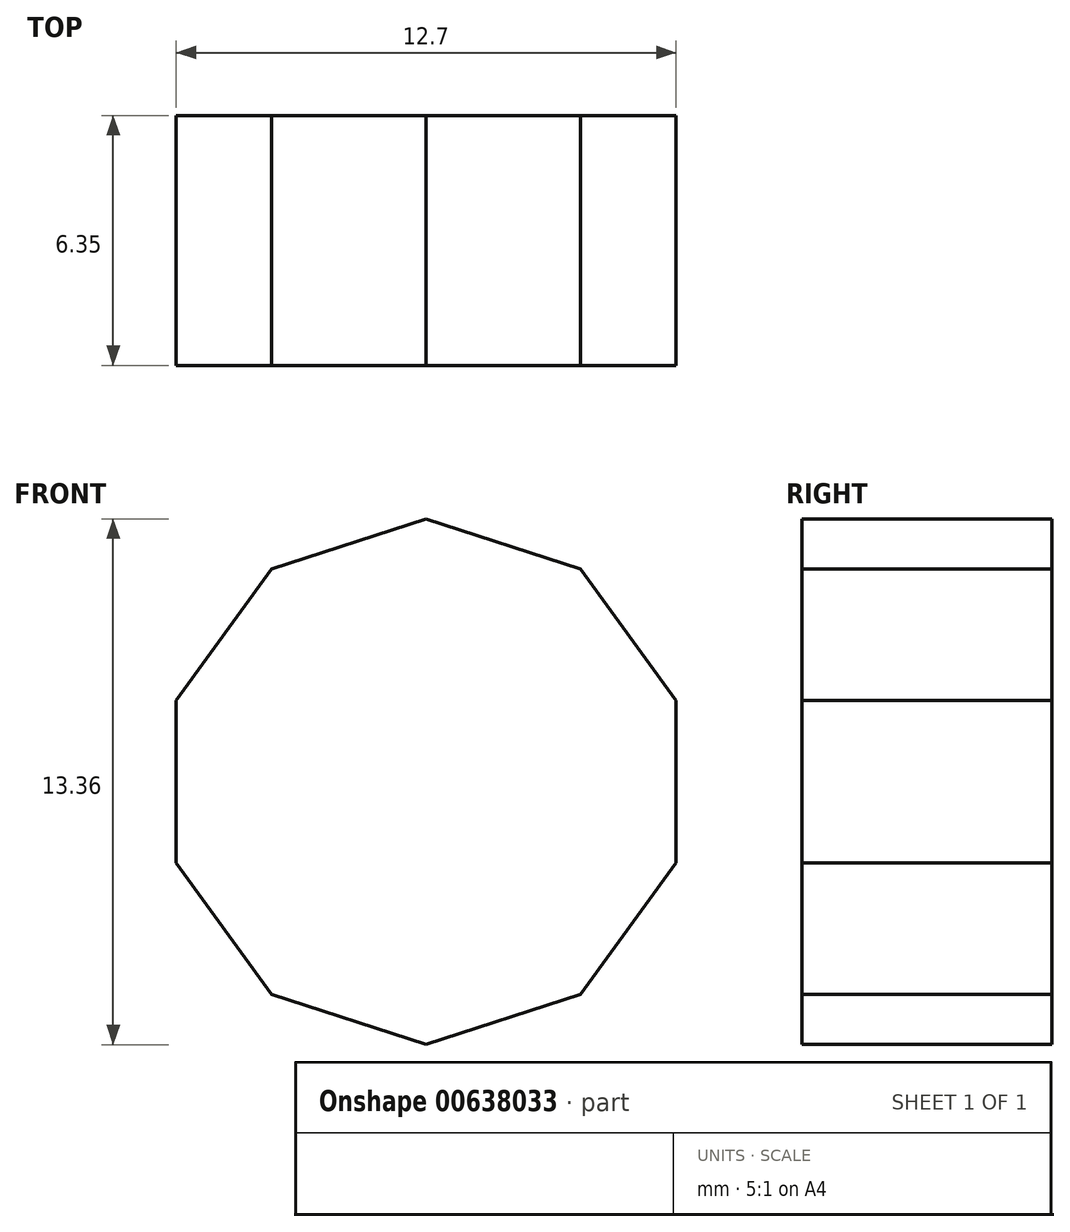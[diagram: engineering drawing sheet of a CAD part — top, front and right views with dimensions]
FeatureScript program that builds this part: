
annotation { "Feature Type Name" : "Feature", "Feature Type Description" : "" }
export const myFeature = defineFeature(function(context is Context, id is Id, definition is map)
    precondition{}
    {
        {
            var Q0;
            Q0=qCreatedBy(makeId("Front.planeOp"),FACE);
            var sketch = newSketch(context, id + "F0", { "sketchPlane" : qUnion([Q0])});
            skCircle(sketch, "E0.cCircle", {"center": v(0, 0) * mm, "radius": 6.35 * mm, "construction": true});
            skLineSegment(sketch, "E0.0", {"start": v(6.35, 2.06) * mm, "end": v(6.35, -2.06) * mm});
            skLineSegment(sketch, "E0.1", {"start": v(6.35, -2.06) * mm, "end": v(3.92, -5.4) * mm});
            skLineSegment(sketch, "E0.2", {"start": v(3.92, -5.4) * mm, "end": v(0, -6.68) * mm});
            skLineSegment(sketch, "E0.3", {"start": v(0, -6.68) * mm, "end": v(-3.92, -5.4) * mm});
            skLineSegment(sketch, "E0.4", {"start": v(-3.92, -5.4) * mm, "end": v(-6.35, -2.06) * mm});
            skLineSegment(sketch, "E0.5", {"start": v(-6.35, -2.06) * mm, "end": v(-6.35, 2.06) * mm});
            skLineSegment(sketch, "E0.6", {"start": v(-6.35, 2.06) * mm, "end": v(-3.92, 5.4) * mm});
            skLineSegment(sketch, "E0.7", {"start": v(-3.92, 5.4) * mm, "end": v(0, 6.68) * mm});
            skLineSegment(sketch, "E0.8", {"start": v(0, 6.68) * mm, "end": v(3.92, 5.4) * mm});
            skLineSegment(sketch, "E0.9", {"start": v(3.92, 5.4) * mm, "end": v(6.35, 2.06) * mm});
            skPoint(sketch, "E0.0.midPoint", {"position": v(6.35, 0) * mm});
            skSolve(sketch);
        }
        {
            var Q0;
            Q0=makeQuery(id+"F0.imprint","IMPRINT",FACE,{"disambiguationData":[TD([[makeQuery(id+"F0.imprint","IMPRINT",EDGE,{"derivedFrom":sQuery(id+"F0.wireOp",EDGE,"E0.0")}),-1.0]])]});
            extrude(context, id + "F1", {"entities" : qUnion([Q0]), "depth" : 6.35 * mm, "offsetDistance" : 25.4 * mm});
        }
        {
            var Q0;
            Q0=makeQuery(id+"F1.opExtrude","SWEPT_FACE",FACE,{"disambiguationData":[OSD([sQuery(id+"F0.wireOp",EDGE,"E0.8")])]});
            var sketch = newSketch(context, id + "F2", { "sketchPlane" : qUnion([Q0])});
            skLineSegment(sketch, "E1", {"start": v(0, 0) * mm, "end": v(0, -6.35) * mm});
            skLineSegment(sketch, "E2", {"start": v(1.63, -1.23) * mm, "end": v(-1.63, -5.12) * mm});
            skPoint(sketch, "E3", {"position": v(0, -3.18) * mm});
            skFitSpline(sketch, "E4", {"points": [v(1.63, -1.23) * mm, v(1.63, -2.95) * mm, v(-1.63, -5.12) * mm, v(-0.55, -4.1) * mm, v(0.85, -2.62) * mm, v(1.63, -1.23) * mm]});
            skSolve(sketch);
        }
        {
            var Q0;
            Q0=makeQuery(id+"F1.opExtrude","SWEPT_FACE",FACE,{"disambiguationData":[OSD([sQuery(id+"F0.wireOp",EDGE,"E0.7")])]});
            var sketch = newSketch(context, id + "F3", { "sketchPlane" : qUnion([Q0])});
            skLineSegment(sketch, "E5", {"start": v(-0.1, 0.06) * mm, "end": v(-0.1, -6.29) * mm});
            skLineSegment(sketch, "E6", {"start": v(1.53, -1.17) * mm, "end": v(-1.74, -5.06) * mm});
            skPoint(sketch, "E7", {"position": v(-0.1, -3.11) * mm});
            skFitSpline(sketch, "E8", {"points": [v(1.53, -1.17) * mm, v(1.53, -2.88) * mm, v(-1.74, -5.06) * mm, v(-0.65, -4.03) * mm, v(0.75, -2.56) * mm, v(1.53, -1.17) * mm]});
            skSolve(sketch);
        }
        {
            var Q0;
            Q0=makeQuery(id+"F1.opExtrude","SWEPT_FACE",FACE,{"disambiguationData":[OSD([sQuery(id+"F0.wireOp",EDGE,"E0.6")])]});
            var sketch = newSketch(context, id + "F4", { "sketchPlane" : qUnion([Q0])});
            skLineSegment(sketch, "E9", {"start": v(-0.02, -0.43) * mm, "end": v(6.33, -0.43) * mm});
            skLineSegment(sketch, "E10", {"start": v(1.21, 1.2) * mm, "end": v(5.1, -2.06) * mm});
            skFitSpline(sketch, "E11", {"points": [v(1.21, 1.2) * mm, v(2.93, 1.2) * mm, v(5.1, -2.06) * mm, v(4.08, -0.98) * mm, v(2.6, 0.42) * mm, v(1.21, 1.2) * mm]});
            skSolve(sketch);
        }
        {
            var Q0;
            Q0=makeQuery(id+"F1.opExtrude","SWEPT_FACE",FACE,{"disambiguationData":[OSD([sQuery(id+"F0.wireOp",EDGE,"E0.5")])]});
            var sketch = newSketch(context, id + "F5", { "sketchPlane" : qUnion([Q0])});
            skLineSegment(sketch, "E12", {"start": v(6.35, 0) * mm, "end": v(0, 0) * mm});
            skLineSegment(sketch, "E13", {"start": v(0.01, 0) * mm, "end": v(6.36, 0) * mm});
            skLineSegment(sketch, "E14", {"start": v(1.24, 1.63) * mm, "end": v(5.13, -1.63) * mm});
            skFitSpline(sketch, "E15", {"points": [v(1.24, 1.63) * mm, v(2.96, 1.63) * mm, v(5.13, -1.63) * mm, v(4.1, -0.55) * mm, v(2.64, 0.85) * mm, v(1.24, 1.63) * mm]});
            skSolve(sketch);
        }
        {
            var Q0;
            Q0=makeQuery(id+"F1.opExtrude","SWEPT_FACE",FACE,{"disambiguationData":[OSD([sQuery(id+"F0.wireOp",EDGE,"E0.4")])]});
            var sketch = newSketch(context, id + "F6", { "sketchPlane" : qUnion([Q0])});
            skLineSegment(sketch, "E16", {"start": v(6.35, 0) * mm, "end": v(0, 0) * mm});
            skLineSegment(sketch, "E17", {"start": v(0, 0) * mm, "end": v(6.34, 0) * mm});
            skLineSegment(sketch, "E18", {"start": v(1.22, 1.63) * mm, "end": v(5.12, -1.63) * mm});
            skFitSpline(sketch, "E19", {"points": [v(1.22, 1.63) * mm, v(2.94, 1.63) * mm, v(5.12, -1.63) * mm, v(4.09, -0.55) * mm, v(2.62, 0.85) * mm, v(1.22, 1.63) * mm]});
            skSolve(sketch);
        }
        {
            var Q0;
            Q0=makeQuery(id+"F1.opExtrude","SWEPT_FACE",FACE,{"disambiguationData":[OSD([sQuery(id+"F0.wireOp",EDGE,"E0.3")])]});
            var sketch = newSketch(context, id + "F7", { "sketchPlane" : qUnion([Q0])});
            skLineSegment(sketch, "E20", {"start": v(0, 6.35) * mm, "end": v(0, 0) * mm});
            skLineSegment(sketch, "E21", {"start": v(0, -0.02) * mm, "end": v(0, 6.33) * mm});
            skLineSegment(sketch, "E22", {"start": v(-1.63, 1.21) * mm, "end": v(1.63, 5.1) * mm});
            skFitSpline(sketch, "E23", {"points": [v(-1.63, 1.21) * mm, v(-1.63, 2.93) * mm, v(1.63, 5.1) * mm, v(0.55, 4.08) * mm, v(-0.85, 2.6) * mm, v(-1.63, 1.21) * mm]});
            skSolve(sketch);
        }
        {
            var Q0;
            Q0=makeQuery(id+"F1.opExtrude","SWEPT_FACE",FACE,{"disambiguationData":[OSD([sQuery(id+"F0.wireOp",EDGE,"E0.2")])]});
            var sketch = newSketch(context, id + "F8", { "sketchPlane" : qUnion([Q0])});
            skLineSegment(sketch, "E24", {"start": v(0, 6.35) * mm, "end": v(0, 0) * mm});
            skLineSegment(sketch, "E25", {"start": v(0, 0) * mm, "end": v(0, 6.36) * mm});
            skLineSegment(sketch, "E26", {"start": v(-1.63, 1.23) * mm, "end": v(1.63, 5.13) * mm});
            skFitSpline(sketch, "E27", {"points": [v(-1.63, 1.23) * mm, v(-1.63, 2.95) * mm, v(1.63, 5.13) * mm, v(0.55, 4.1) * mm, v(-0.85, 2.63) * mm, v(-1.63, 1.23) * mm]});
            skSolve(sketch);
        }
        {
            var Q0;
            Q0=makeQuery(id+"F1.opExtrude","SWEPT_FACE",FACE,{"disambiguationData":[OSD([sQuery(id+"F0.wireOp",EDGE,"E0.1")])]});
            var sketch = newSketch(context, id + "F9", { "sketchPlane" : qUnion([Q0])});
            skLineSegment(sketch, "E28", {"start": v(-6.35, 0) * mm, "end": v(0, 0) * mm});
            skLineSegment(sketch, "E29", {"start": v(0, 0) * mm, "end": v(-6.35, 0) * mm});
            skLineSegment(sketch, "E30", {"start": v(-1.23, -1.63) * mm, "end": v(-5.12, 1.63) * mm});
            skFitSpline(sketch, "E31", {"points": [v(-1.23, -1.63) * mm, v(-2.95, -1.63) * mm, v(-5.12, 1.63) * mm, v(-4.1, 0.55) * mm, v(-2.62, -0.85) * mm, v(-1.23, -1.63) * mm]});
            skSolve(sketch);
        }
        {
            var Q0;
            Q0=makeQuery(id+"F1.opExtrude","SWEPT_FACE",FACE,{"disambiguationData":[OSD([sQuery(id+"F0.wireOp",EDGE,"E0.0")])]});
            var sketch = newSketch(context, id + "F10", { "sketchPlane" : qUnion([Q0])});
            skLineSegment(sketch, "E32", {"start": v(-6.35, 0) * mm, "end": v(0, 0) * mm});
            skLineSegment(sketch, "E33", {"start": v(0, 0) * mm, "end": v(-6.34, 0) * mm});
            skLineSegment(sketch, "E34", {"start": v(-1.22, -1.63) * mm, "end": v(-5.11, 1.63) * mm});
            skFitSpline(sketch, "E35", {"points": [v(-1.22, -1.63) * mm, v(-2.94, -1.63) * mm, v(-5.11, 1.63) * mm, v(-4.09, 0.55) * mm, v(-2.62, -0.85) * mm, v(-1.22, -1.63) * mm]});
            skSolve(sketch);
        }
        {
            var Q0;
            Q0=makeQuery(id+"F1.opExtrude","SWEPT_FACE",FACE,{"disambiguationData":[OSD([sQuery(id+"F0.wireOp",EDGE,"E0.9")])]});
            var sketch = newSketch(context, id + "F11", { "sketchPlane" : qUnion([Q0])});
            skLineSegment(sketch, "E36", {"start": v(-6.35, 0) * mm, "end": v(0, 0) * mm});
            skLineSegment(sketch, "E37", {"start": v(0, 0) * mm, "end": v(-6.36, 0) * mm});
            skLineSegment(sketch, "E38", {"start": v(-1.24, -1.63) * mm, "end": v(-5.13, 1.63) * mm});
            skFitSpline(sketch, "E39", {"points": [v(-1.24, -1.63) * mm, v(-2.95, -1.63) * mm, v(-5.13, 1.63) * mm, v(-4.1, 0.55) * mm, v(-2.63, -0.85) * mm, v(-1.24, -1.63) * mm]});
            skSolve(sketch);
        }
        {
            var Q0;
            Q0=sQuery(id+"F7.wireOp",EDGE,"E23");
            extrude(context, id + "F12", {"bodyType" : ToolBodyType.SURFACE, "surfaceEntities" : qUnion([Q0]), "depth" : 30.48 * mm, "offsetDistance" : 25.4 * mm});
        }
        {
            var Q0;
            Q0=sQuery(id+"F8.wireOp",EDGE,"E27");
            extrude(context, id + "F13", {"bodyType" : ToolBodyType.SURFACE, "surfaceEntities" : qUnion([Q0]), "depth" : 30.48 * mm, "offsetDistance" : 25.4 * mm});
        }
        {
            var Q0;
            Q0=sQuery(id+"F9.wireOp",EDGE,"E31");
            extrude(context, id + "F14", {"bodyType" : ToolBodyType.SURFACE, "surfaceEntities" : qUnion([Q0]), "depth" : 30.48 * mm, "offsetDistance" : 25.4 * mm});
        }
        {
            var Q0;
            Q0=sQuery(id+"F10.wireOp",EDGE,"E35");
            extrude(context, id + "F15", {"bodyType" : ToolBodyType.SURFACE, "surfaceEntities" : qUnion([Q0]), "depth" : 30.48 * mm, "offsetDistance" : 25.4 * mm});
        }
        {
            var Q0;
            Q0=sQuery(id+"F11.wireOp",EDGE,"E39");
            extrude(context, id + "F16", {"bodyType" : ToolBodyType.SURFACE, "surfaceEntities" : qUnion([Q0]), "depth" : 30.48 * mm, "offsetDistance" : 25.4 * mm});
        }
        {
            var Q0;
            Q0=sQuery(id+"F2.wireOp",EDGE,"E4");
            extrude(context, id + "F17", {"bodyType" : ToolBodyType.SURFACE, "surfaceEntities" : qUnion([Q0]), "depth" : 30.48 * mm, "offsetDistance" : 25.4 * mm});
        }
        {
            var Q0;
            Q0=sQuery(id+"F3.wireOp",EDGE,"E8");
            extrude(context, id + "F18", {"bodyType" : ToolBodyType.SURFACE, "surfaceEntities" : qUnion([Q0]), "depth" : 30.48 * mm, "offsetDistance" : 25.4 * mm});
        }
        {
            var Q0;
            Q0=sQuery(id+"F4.wireOp",EDGE,"E11");
            extrude(context, id + "F19", {"bodyType" : ToolBodyType.SURFACE, "surfaceEntities" : qUnion([Q0]), "depth" : 30.48 * mm, "offsetDistance" : 25.4 * mm});
        }
        {
            var Q0;
            Q0=sQuery(id+"F5.wireOp",EDGE,"E15");
            extrude(context, id + "F20", {"bodyType" : ToolBodyType.SURFACE, "surfaceEntities" : qUnion([Q0]), "depth" : 30.48 * mm, "offsetDistance" : 25.4 * mm});
        }
        {
            var Q0;
            Q0=sQuery(id+"F6.wireOp",EDGE,"E19");
            extrude(context, id + "F21", {"bodyType" : ToolBodyType.SURFACE, "surfaceEntities" : qUnion([Q0]), "depth" : 30.48 * mm, "offsetDistance" : 25.4 * mm});
        }
    });
